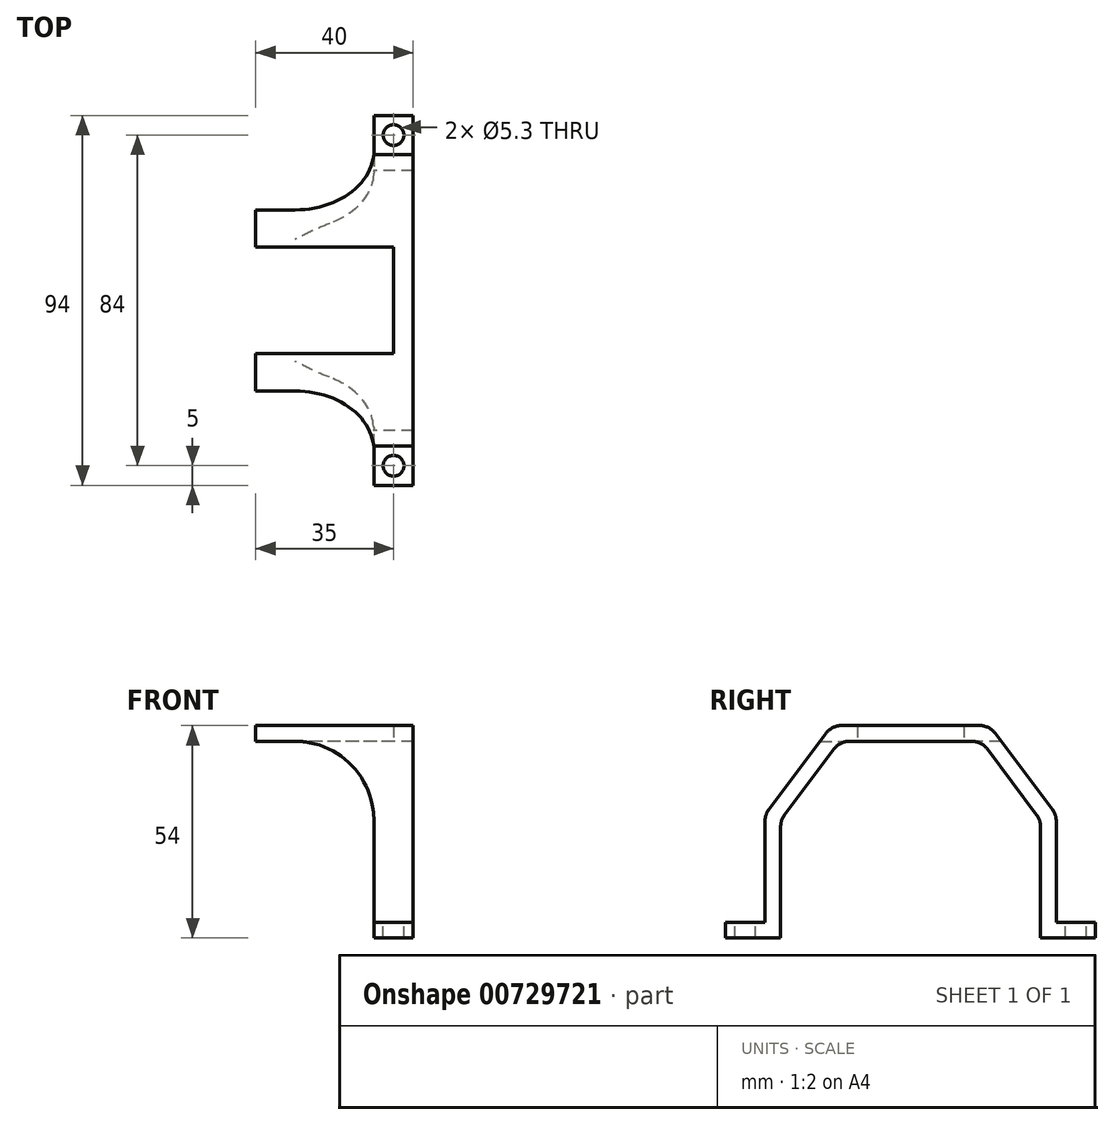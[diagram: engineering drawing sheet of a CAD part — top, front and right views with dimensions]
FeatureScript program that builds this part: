
annotation { "Feature Type Name" : "Feature", "Feature Type Description" : "" }
export const myFeature = defineFeature(function(context is Context, id is Id, definition is map)
    precondition{}
    {
        {
            var Q0;
            Q0=qCreatedBy(makeId("Right.planeOp"),FACE);
            var sketch = newSketch(context, id + "F0", { "sketchPlane" : qUnion([Q0])});
            skLineSegment(sketch, "E0", {"start": v(-47, 0) * mm, "end": v(-33, 0) * mm});
            skLineSegment(sketch, "E1", {"start": v(-33, 0) * mm, "end": v(-33, 30) * mm});
            skLineSegment(sketch, "E2", {"start": v(-33, 30) * mm, "end": v(-18, 50) * mm});
            skLineSegment(sketch, "E3", {"start": v(-18, 50) * mm, "end": v(0, 50) * mm});
            skLineSegment(sketch, "E4", {"start": v(0, 50) * mm, "end": v(0, 54) * mm});
            skLineSegment(sketch, "E5", {"start": v(0, 54) * mm, "end": v(-20, 54) * mm});
            skLineSegment(sketch, "E6", {"start": v(-20, 54) * mm, "end": v(-37, 31.33) * mm});
            skLineSegment(sketch, "E7", {"start": v(-37, 31.33) * mm, "end": v(-37, 4) * mm});
            skLineSegment(sketch, "E8", {"start": v(-37, 4) * mm, "end": v(-47, 4) * mm});
            skLineSegment(sketch, "E9", {"start": v(-47, 4) * mm, "end": v(-47, 0) * mm});
            skSolve(sketch);
        }
        {
            var Q0;
            Q0=makeQuery(id+"F0.imprint","IMPRINT",FACE,{"disambiguationData":[TD([[makeQuery(id+"F0.imprint","IMPRINT",EDGE,{"derivedFrom":sQuery(id+"F0.wireOp",EDGE,"E0")}),1.0]])]});
            extrude(context, id + "F1", {"entities" : qUnion([Q0]), "endBound" : BoundingType.SYMMETRIC, "depth" : 40 * mm, "offsetDistance" : 25 * mm});
        }
        {
            var Q0;
            Q0=makeQuery(id+"F1.opExtrude","CAP_FACE",FACE,{"disambiguationData":[OSD([sQuery(id+"F0.wireOp",EDGE,"E0"),sQuery(id+"F0.wireOp",EDGE,"E1"),sQuery(id+"F0.wireOp",EDGE,"E2"),sQuery(id+"F0.wireOp",EDGE,"E3"),sQuery(id+"F0.wireOp",EDGE,"E4"),sQuery(id+"F0.wireOp",EDGE,"E5"),sQuery(id+"F0.wireOp",EDGE,"E6"),sQuery(id+"F0.wireOp",EDGE,"E7"),sQuery(id+"F0.wireOp",EDGE,"E8"),sQuery(id+"F0.wireOp",EDGE,"E9")])],"isStart":true});
            var sketch = newSketch(context, id + "F2", { "sketchPlane" : qUnion([Q0])});
            skLineSegment(sketch, "E10.bottom", {"start": v(47, 0) * mm, "end": v(0, 0) * mm});
            skLineSegment(sketch, "E10.top", {"start": v(47, 50) * mm, "end": v(0, 50) * mm});
            skLineSegment(sketch, "E10.left", {"start": v(47, 0) * mm, "end": v(47, 50) * mm});
            skLineSegment(sketch, "E10.right", {"start": v(0, 0) * mm, "end": v(0, 50) * mm});
            skSolve(sketch);
        }
        {
            var Q0;
            {var subQ6=makeQuery(id+"F1.opExtrude","CAP_EDGE",EDGE,{"disambiguationData":[OSD([sQuery(id+"F0.wireOp",EDGE,"E7")])],"isStart":true});Q0=makeQuery(id+"F2.imprint","IMPRINT",FACE,{"disambiguationData":[TD([[makeQuery(id+"F2.imprint","IMPRINT",EDGE,{"derivedFrom":subQ6}),1.0]])]});}
            var Q1;
            {var subQ0=makeQuery(id+"F1.opExtrude","CAP_EDGE",EDGE,{"disambiguationData":[OSD([sQuery(id+"F0.wireOp",EDGE,"E1")])],"isStart":true});Q1=makeQuery(id+"F2.imprint","IMPRINT",FACE,{"disambiguationData":[TD([[makeQuery(id+"F2.imprint","IMPRINT",EDGE,{"derivedFrom":subQ0}),-1.0]])]});}
            var Q2;
            {var subQ0=sQuery(id+"F2.wireOp",EDGE,"E10.right");Q2=makeQuery(id+"F2.imprint","IMPRINT",FACE,{"disambiguationData":[TD([[makeQuery(id+"F2.imprint","IMPRINT",EDGE,{"derivedFrom":subQ0}),-1.0]])]});}
            extrude(context, id + "F3", {"entities" : qUnion([Q0, Q1, Q2]), "operationType" : NewBodyOperationType.REMOVE, "oppositeDirection" : true, "depth" : 30 * mm, "offsetDistance" : 25 * mm});
        }
        {
            var Q0;
            Q0=makeQuery(id+"F3.boolean.opBoolean","COPY",EDGE,{"derivedFrom":makeQuery(id+"F3.opExtrude","CAP_EDGE",EDGE,{"disambiguationData":[OSD([sQuery(id+"F2.wireOp",EDGE,"E10.top")])],"isStart":false})});
            fillet(context, id + "F4", {"entities" : qUnion([Q0]), "radius" : 20 * mm, "tangentPropagation" : true, "allowEdgeOverflow" : false});
        }
        {
            var Q0;
            Q0=makeQuery(id+"F1.opExtrude","CAP_FACE",FACE,{"disambiguationData":[OSD([sQuery(id+"F0.wireOp",EDGE,"E0"),sQuery(id+"F0.wireOp",EDGE,"E1"),sQuery(id+"F0.wireOp",EDGE,"E2"),sQuery(id+"F0.wireOp",EDGE,"E3"),sQuery(id+"F0.wireOp",EDGE,"E4"),sQuery(id+"F0.wireOp",EDGE,"E5"),sQuery(id+"F0.wireOp",EDGE,"E6"),sQuery(id+"F0.wireOp",EDGE,"E7"),sQuery(id+"F0.wireOp",EDGE,"E8"),sQuery(id+"F0.wireOp",EDGE,"E9")])],"isStart":true});
            var sketch = newSketch(context, id + "F5", { "sketchPlane" : qUnion([Q0])});
            skLineSegment(sketch, "E11.bottom", {"start": v(0, 54) * mm, "end": v(13.5, 54) * mm});
            skLineSegment(sketch, "E11.top", {"start": v(0, 50) * mm, "end": v(13.5, 50) * mm});
            skLineSegment(sketch, "E11.left", {"start": v(0, 54) * mm, "end": v(0, 50) * mm});
            skLineSegment(sketch, "E11.right", {"start": v(13.5, 54) * mm, "end": v(13.5, 50) * mm});
            skSolve(sketch);
        }
        {
            var Q0;
            Q0=makeQuery(id+"F5.imprint","IMPRINT",FACE,{"disambiguationData":[TD([[makeQuery(id+"F5.imprint","IMPRINT",EDGE,{"derivedFrom":sQuery(id+"F5.wireOp",EDGE,"E11.bottom")}),-1.0]])]});
            extrude(context, id + "F6", {"entities" : qUnion([Q0]), "operationType" : NewBodyOperationType.REMOVE, "oppositeDirection" : true, "depth" : 35 * mm, "offsetDistance" : 25 * mm});
        }
        {
            var Q0;
            Q0=makeQuery(id+"F1.opExtrude","SWEPT_FACE",FACE,{"disambiguationData":[OSD([sQuery(id+"F0.wireOp",EDGE,"E8")])]});
            var sketch = newSketch(context, id + "F7", { "sketchPlane" : qUnion([Q0])});
            skCircle(sketch, "E12", {"center": v(15, -42) * mm, "radius": 2.65 * mm});
            skLineSegment(sketch, "E13", {"start": v(15, -47) * mm, "end": v(15, -35.9) * mm, "construction": true});
            skSolve(sketch);
        }
        {
            var Q0;
            Q0=makeQuery(id+"F7.imprint","IMPRINT",FACE,{"disambiguationData":[TD([[makeQuery(id+"F7.imprint","IMPRINT",EDGE,{"derivedFrom":sQuery(id+"F7.wireOp",EDGE,"E12")}),1.0]])]});
            extrude(context, id + "F8", {"entities" : qUnion([Q0]), "operationType" : NewBodyOperationType.REMOVE, "endBound" : BoundingType.THROUGH_ALL, "oppositeDirection" : true, "depth" : 25 * mm, "offsetDistance" : 25 * mm});
        }
        {
            var Q0;
            Q0=makeQuery(id+"F1.opExtrude","SWEPT_BODY",BODY,{"disambiguationData":[OSD([sQuery(id+"F0.wireOp",EDGE,"E0"),sQuery(id+"F0.wireOp",EDGE,"E1"),sQuery(id+"F0.wireOp",EDGE,"E2"),sQuery(id+"F0.wireOp",EDGE,"E3"),sQuery(id+"F0.wireOp",EDGE,"E4"),sQuery(id+"F0.wireOp",EDGE,"E5"),sQuery(id+"F0.wireOp",EDGE,"E6"),sQuery(id+"F0.wireOp",EDGE,"E7"),sQuery(id+"F0.wireOp",EDGE,"E8"),sQuery(id+"F0.wireOp",EDGE,"E9")])]});
            var Q1;
            Q1=qCreatedBy(makeId("Front.planeOp"),FACE);
            mirror(context, id + "F9", {"operationType" : NewBodyOperationType.ADD, "entities" : qUnion([Q0]), "mirrorPlane" : qUnion([Q1])});
        }
        {
            var Q0;
            Q0=makeQuery(id+"F1.opExtrude","SWEPT_EDGE",EDGE,{"disambiguationData":[OSD([sQuery(id+"F0.wireOp",EDGE,"E5"),sQuery(id+"F0.wireOp",EDGE,"E6")])]});
            var Q1;
            Q1=makeQuery(id+"F1.opExtrude","SWEPT_EDGE",EDGE,{"disambiguationData":[OSD([sQuery(id+"F0.wireOp",EDGE,"E6"),sQuery(id+"F0.wireOp",EDGE,"E7")])]});
            var Q2;
            Q2=makeQuery(id+"F9.opPattern","COPY",EDGE,{"derivedFrom":makeQuery(id+"F1.opExtrude","SWEPT_EDGE",EDGE,{"disambiguationData":[OSD([sQuery(id+"F0.wireOp",EDGE,"E1"),sQuery(id+"F0.wireOp",EDGE,"E2")])]}),"instanceName":"1"});
            var Q3;
            Q3=makeQuery(id+"F9.opPattern","COPY",EDGE,{"derivedFrom":makeQuery(id+"F1.opExtrude","SWEPT_EDGE",EDGE,{"disambiguationData":[OSD([sQuery(id+"F0.wireOp",EDGE,"E5"),sQuery(id+"F0.wireOp",EDGE,"E6")])]}),"instanceName":"1"});
            var Q4;
            Q4=makeQuery(id+"F1.opExtrude","SWEPT_EDGE",EDGE,{"disambiguationData":[OSD([sQuery(id+"F0.wireOp",EDGE,"E1"),sQuery(id+"F0.wireOp",EDGE,"E2")])]});
            var Q5;
            Q5=makeQuery(id+"F9.opPattern","COPY",EDGE,{"derivedFrom":makeQuery(id+"F1.opExtrude","SWEPT_EDGE",EDGE,{"disambiguationData":[OSD([sQuery(id+"F0.wireOp",EDGE,"E6"),sQuery(id+"F0.wireOp",EDGE,"E7")])]}),"instanceName":"1"});
            var Q6;
            Q6=makeQuery(id+"F9.opPattern","COPY",EDGE,{"derivedFrom":makeQuery(id+"F1.opExtrude","SWEPT_EDGE",EDGE,{"disambiguationData":[OSD([sQuery(id+"F0.wireOp",EDGE,"E2"),sQuery(id+"F0.wireOp",EDGE,"E3")])]}),"instanceName":"1"});
            var Q7;
            Q7=makeQuery(id+"F1.opExtrude","SWEPT_EDGE",EDGE,{"disambiguationData":[OSD([sQuery(id+"F0.wireOp",EDGE,"E2"),sQuery(id+"F0.wireOp",EDGE,"E3")])]});
            fillet(context, id + "F10", {"entities" : qUnion([Q0, Q1, Q2, Q3, Q4, Q5, Q6, Q7]), "radius" : 5 * mm, "tangentPropagation" : true, "allowEdgeOverflow" : false});
        }
    });
